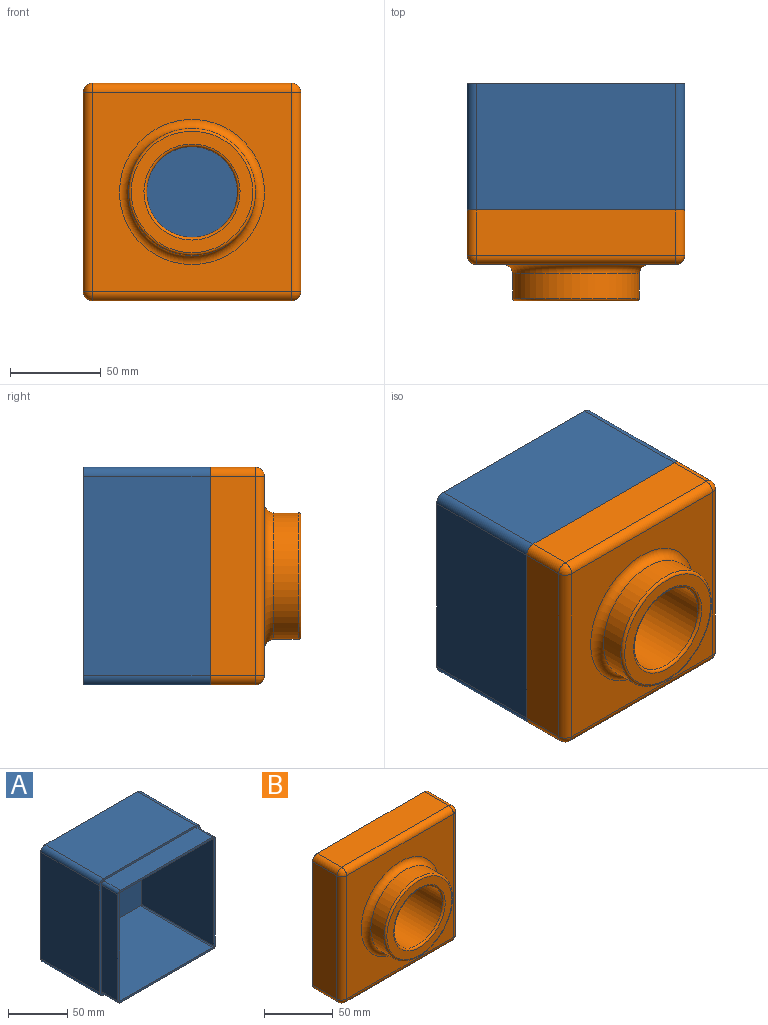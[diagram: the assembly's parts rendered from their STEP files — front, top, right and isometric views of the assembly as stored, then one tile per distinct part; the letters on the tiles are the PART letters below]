
ASSEMBLY  parts=2 mates=1
PART A: 28 faces, bbox 120x90x120 mm
  f0: plane 116x116mm, normal (0,-1,0), area 905.1mm2, adj f1,f2,f3,f4,f6,f7,f8,f9
  f1: plane 110x86mm, normal (0,0,-1), area 9460mm2, adj f0,f5,f6,f9
  f2: plane 110x86mm, normal (1,0,0), area 9460mm2, adj f0,f5,f6,f7
  f3: plane 110x86mm, normal (0,0,1), area 9460mm2, adj f0,f5,f7,f8
  f4: plane 110x86mm, normal (-1,0,0), area 9460mm2, adj f0,f5,f8,f9
  f5: plane 112x112mm, normal (0,-1,0), area 12543.1mm2, adj f1,f2,f3,f4,f6,f7,f8,f9
  f6: cylinder r=1mm len=86mm, axis (0,-1,0), area 135.1mm2, adj f0,f1,f2,f5
  f7: cylinder r=1mm len=86mm, axis (0,1,0), area 135.1mm2, adj f0,f2,f3,f5
  f8: cylinder r=1mm len=86mm, axis (0,-1,0), area 135.1mm2, adj f0,f3,f4,f5
  f9: cylinder r=1mm len=86mm, axis (0,1,0), area 135.1mm2, adj f0,f1,f4,f5
  f10: cylinder r=3mm len=20mm, axis (0,-1,0), area 94.2mm2, adj f0,f11,f17,f18
  f11: plane 110x20mm, normal (1,0,0), area 2200mm2, adj f0,f10,f12,f18
  f12: cylinder r=3mm len=20mm, axis (0,-1,0), area 94.2mm2, adj f0,f11,f13,f18
  f13: plane 110x20mm, normal (0,0,-1), area 2200mm2, adj f0,f12,f14,f18
  f14: cylinder r=3mm len=20mm, axis (0,-1,0), area 94.2mm2, adj f0,f13,f15,f18
  f15: plane 110x20mm, normal (-1,0,0), area 2200mm2, adj f0,f14,f16,f18
  f16: cylinder r=3mm len=20mm, axis (0,-1,0), area 94.2mm2, adj f0,f15,f17,f18
  f17: plane 110x20mm, normal (0,0,1), area 2200mm2, adj f0,f10,f16,f18
  f18: plane 120x120mm, normal (0,-1,0), area 930.3mm2, adj f10,f11,f12,f13,f14,f15,f16,f17
  f19: plane 120x120mm, normal (0,1,0), area 14378.5mm2, adj f20,f21,f22,f23,f24,f25,f26,f27
  f20: cylinder r=5mm len=70mm, axis (0,-1,0), area 549.8mm2, adj f18,f19,f22,f24
  f21: cylinder r=5mm len=70mm, axis (0,1,0), area 549.8mm2, adj f18,f19,f22,f27
  f22: plane 110x70mm, normal (1,0,0), area 7700mm2, adj f18,f19,f20,f21
  f23: cylinder r=5mm len=70mm, axis (0,1,0), area 549.8mm2, adj f18,f19,f24,f26
  f24: plane 110x70mm, normal (0,0,-1), area 7700mm2, adj f18,f19,f20,f23
  f25: cylinder r=5mm len=70mm, axis (0,-1,0), area 549.8mm2, adj f18,f19,f26,f27
  f26: plane 110x70mm, normal (-1,0,0), area 7700mm2, adj f18,f19,f23,f25
  f27: plane 110x70mm, normal (0,0,1), area 7700mm2, adj f18,f19,f21,f25
PART B: 46 faces, bbox 120x50x120 mm
  f0: plane 120x120mm, normal (0,1,0), area 930.3mm2, adj f1,f2,f3,f4,f11,f13,f16,f22
  f1: plane 110x25mm, normal (-1,0,0), area 2750mm2, adj f0,f13,f19,f22
  f2: plane 110x25mm, normal (0,0,-1), area 2750mm2, adj f0,f16,f20,f22
  f3: plane 110x25mm, normal (1,0,0), area 2750mm2, adj f0,f11,f15,f16
  f4: plane 110x25mm, normal (0,0,1), area 2750mm2, adj f0,f11,f13,f14
  f5: plane 110x110mm, normal (0,-1,0), area 7073.5mm2, adj f10,f14,f15,f19,f20
  f6: plane 54x54mm, normal (0,1,0), area 326.7mm2, adj f9,f32
  f7: cylinder r=35mm len=70mm, axis (0,1,0), area 2968.8mm2, adj f10,f24
  f8: plane 67x67mm, normal (0,-1,0), area 1319.5mm2, adj f23,f24
  f9: cylinder r=25mm len=50mm, axis (0,-1,0), area 7618.4mm2, adj f6,f23
  f10: torus R=40mm, axis (0,-1,0), area 1816.8mm2, adj f5,f7
  f11: cylinder r=5mm len=25mm, axis (0,-1,0), area 196.3mm2, adj f0,f3,f4,f12
  f12: sphere r=5mm, area 39.3mm2, adj f11,f14,f15
  f13: cylinder r=5mm len=25mm, axis (0,1,0), area 196.3mm2, adj f0,f1,f4,f17
  f14: cylinder r=5mm len=110mm, axis (1,0,0), area 863.9mm2, adj f4,f5,f12,f17
  f15: cylinder r=5mm len=110mm, axis (0,0,-1), area 863.9mm2, adj f3,f5,f12,f18
  f16: cylinder r=5mm len=25mm, axis (0,1,0), area 196.3mm2, adj f0,f2,f3,f18
  f17: sphere r=5mm, area 39.3mm2, adj f13,f14,f19
  f18: sphere r=5mm, area 39.3mm2, adj f15,f16,f20
  f19: cylinder r=5mm len=110mm, axis (0,0,1), area 863.9mm2, adj f1,f5,f17,f21
  f20: cylinder r=5mm len=110mm, axis (-1,0,0), area 863.9mm2, adj f2,f5,f18,f21
  f21: sphere r=5mm, area 39.3mm2, adj f19,f20,f22
  f22: cylinder r=5mm len=25mm, axis (0,-1,0), area 196.3mm2, adj f0,f1,f2,f21
  f23: torus R=26.5mm, axis (0,-1,0), area 378.2mm2, adj f8,f9
  f24: torus R=33.5mm, axis (0,-1,0), area 510.1mm2, adj f7,f8
  f25: plane 110x25mm, normal (1,0,0), area 2750mm2, adj f0,f36,f42,f45
  f26: plane 110x25mm, normal (0,0,1), area 2750mm2, adj f0,f39,f43,f45
  f27: plane 110x25mm, normal (-1,0,0), area 2750mm2, adj f0,f34,f38,f39
  f28: plane 110x25mm, normal (0,0,-1), area 2750mm2, adj f0,f34,f36,f37
  f29: plane 110x110mm, normal (0,1,0), area 7073.5mm2, adj f33,f37,f38,f42,f43
  f30: cylinder r=33mm len=66mm, axis (0,1,0), area 2695.5mm2, adj f31,f33
  f31: plane 66x66mm, normal (0,1,0), area 1131mm2, adj f30,f32
  f32: cylinder r=27mm len=54mm, axis (0,-1,0), area 8143mm2, adj f6,f31
  f33: torus R=40mm, axis (0,-1,0), area 2455.6mm2, adj f29,f30
  f34: cylinder r=3mm len=25mm, axis (0,-1,0), area 117.8mm2, adj f0,f27,f28,f35
  f35: sphere r=3mm, area 14.1mm2, adj f34,f37,f38
  f36: cylinder r=3mm len=25mm, axis (0,1,0), area 117.8mm2, adj f0,f25,f28,f40
  f37: cylinder r=3mm len=110mm, axis (1,0,0), area 518.4mm2, adj f28,f29,f35,f40
  f38: cylinder r=3mm len=110mm, axis (0,0,-1), area 518.4mm2, adj f27,f29,f35,f41
  f39: cylinder r=3mm len=25mm, axis (0,1,0), area 117.8mm2, adj f0,f26,f27,f41
  f40: sphere r=3mm, area 14.1mm2, adj f36,f37,f42
  f41: sphere r=3mm, area 14.1mm2, adj f38,f39,f43
  f42: cylinder r=3mm len=110mm, axis (0,0,1), area 518.4mm2, adj f25,f29,f40,f44
  f43: cylinder r=3mm len=110mm, axis (-1,0,0), area 518.4mm2, adj f26,f29,f41,f44
  f44: sphere r=3mm, area 14.1mm2, adj f42,f43,f45
  f45: cylinder r=3mm len=25mm, axis (0,-1,0), area 117.8mm2, adj f0,f25,f26,f44
PLACE A t=(-60,4,60)mm fixed
PLACE B t=(-60,-66,-60)mm
MATE fastened A.f18 <-> B.f0  axis (0,-1,0) through (0,-66,60)mm
